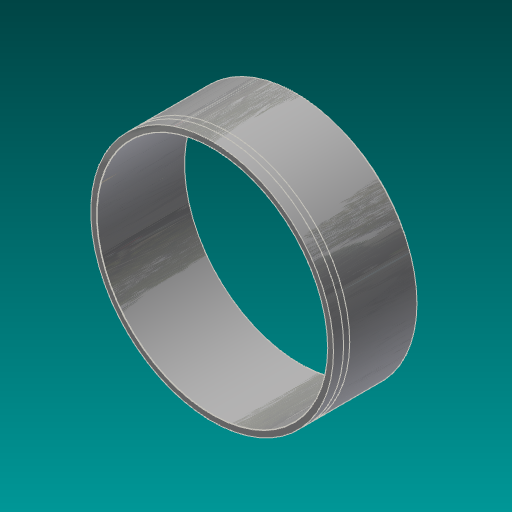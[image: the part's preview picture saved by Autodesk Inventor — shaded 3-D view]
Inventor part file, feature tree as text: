
AUTODESK INVENTOR PART (.ipt)
format: ipt  version: 2017.3 (Build 213256000, 256)  size: 173,568 bytes
history: native  units: in
note: dims shown in document units (in); Inventor stores cm internally (conversion verified against a paired STEP export)
features: chamfer x2, plane x2, split x2, extrude x1, sketch x1
ambient origin geometry x8: Origin, YZ Plane, XZ Plane, XY Plane, X Axis, Y Axis, Z Axis, Center Point
bodies: Solid1 (feature_tree)
feature tree (8):
  extrude  "Extrusion1"  Depth=10.8438in
  chamfer  "Chamfer1"  Distance=10.8438in
  plane  "Work Plane2"
  split  "Split1"
  split  "Split2"
  chamfer  "Chamfer2"  Distance=0.6875in
  sketch  "Sketch1"  dims[d0=30.0in d1=28.5in d2=10.8438in d3=0.0in d4=0.6875in d5=0.125in d6=0.2577in d7=-2.0in d8=0.75in d9=0.0312in d10=0.125in d11=45.0deg]
  plane  "Work Plane1"
